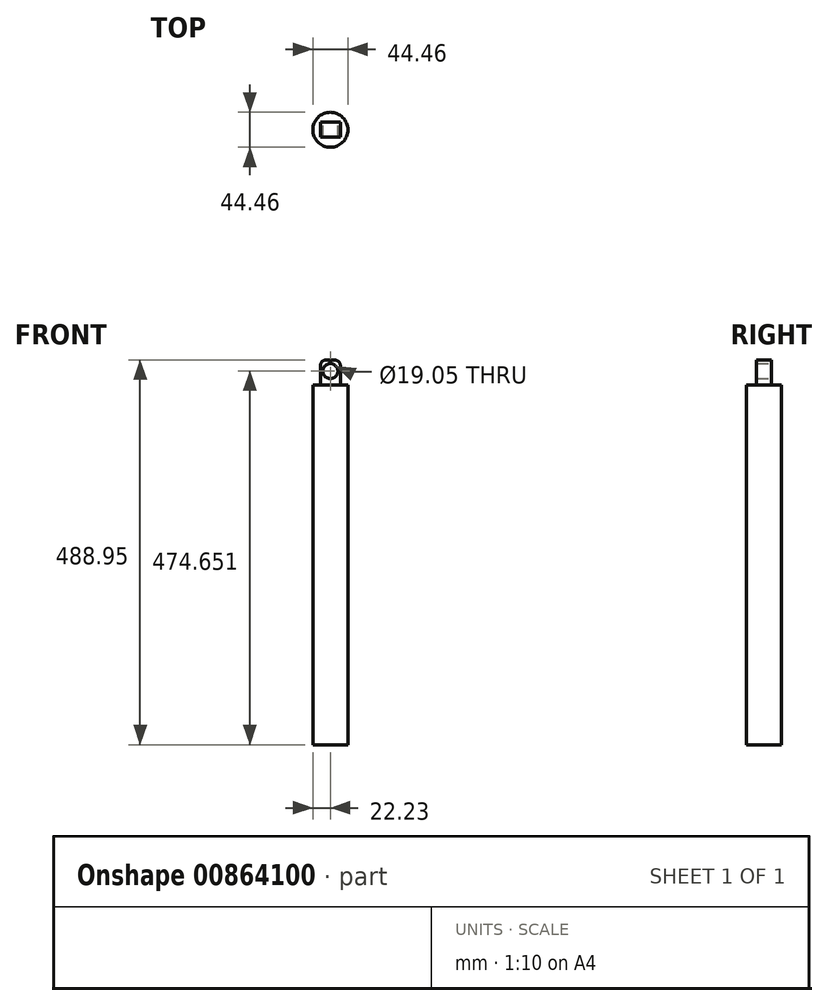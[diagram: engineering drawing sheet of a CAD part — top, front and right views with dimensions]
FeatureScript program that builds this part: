
annotation { "Feature Type Name" : "Feature", "Feature Type Description" : "" }
export const myFeature = defineFeature(function(context is Context, id is Id, definition is map)
    precondition{}
    {
        {
            var Q0;
            Q0=qCreatedBy(makeId("Top.planeOp"),FACE);
            var sketch = newSketch(context, id + "F0", { "sketchPlane" : qUnion([Q0])});
            skCircle(sketch, "E0", {"center": v(0, 0) * mm, "radius": 22.23 * mm});
            skSolve(sketch);
        }
        {
            var Q0;
            Q0=makeQuery(id+"F0.imprint","IMPRINT",FACE,{"disambiguationData":[TD([[makeQuery(id+"F0.imprint","IMPRINT",EDGE,{"derivedFrom":sQuery(id+"F0.wireOp",EDGE,"E0")}),1.0]])]});
            extrude(context, id + "F1", {"entities" : qUnion([Q0]), "oppositeDirection" : true, "depth" : 457.2 * mm, "offsetDistance" : 25.4 * mm});
        }
        {
            var Q0;
            Q0=qCreatedBy(makeId("Front.planeOp"),FACE);
            var sketch = newSketch(context, id + "F2", { "sketchPlane" : qUnion([Q0])});
            skLineSegment(sketch, "E1.bottom", {"start": v(12.7, -31.75) * mm, "end": v(-12.7, -31.75) * mm});
            skLineSegment(sketch, "E1.top", {"start": v(12.7, 31.75) * mm, "end": v(-12.7, 31.75) * mm});
            skLineSegment(sketch, "E1.left", {"start": v(12.7, -31.75) * mm, "end": v(12.7, 31.75) * mm});
            skLineSegment(sketch, "E1.right", {"start": v(-12.7, -31.75) * mm, "end": v(-12.7, 31.75) * mm});
            skPoint(sketch, "E1.middle", {"position": v(0, 0) * mm});
            skCircle(sketch, "E2", {"center": v(0, 17.45) * mm, "radius": 9.53 * mm});
            skSolve(sketch);
        }
        {
            var Q0;
            Q0=makeQuery(id+"F2.imprint","IMPRINT",FACE,{"disambiguationData":[TD([[makeQuery(id+"F2.imprint","IMPRINT",EDGE,{"derivedFrom":sQuery(id+"F2.wireOp",EDGE,"E1.bottom")}),-1.0]])]});
            extrude(context, id + "F3", {"entities" : qUnion([Q0]), "operationType" : NewBodyOperationType.ADD, "depth" : 19.05 * mm, "offsetDistance" : 25.4 * mm, "symmetric" : true});
        }
        {
            var Q0;
            Q0=makeQuery(id+"F3.opExtrude","SWEPT_EDGE",EDGE,{"disambiguationData":[OSD([sQuery(id+"F2.wireOp",EDGE,"E1.top"),sQuery(id+"F2.wireOp",EDGE,"E1.left")])]});
            var Q1;
            Q1=makeQuery(id+"F3.opExtrude","SWEPT_EDGE",EDGE,{"disambiguationData":[OSD([sQuery(id+"F2.wireOp",EDGE,"E1.top"),sQuery(id+"F2.wireOp",EDGE,"E1.right")])]});
            fillet(context, id + "F4", {"entities" : qUnion([Q0, Q1]), "radius" : 7.62 * mm, "tangentPropagation" : true, "allowEdgeOverflow" : false});
        }
    });
